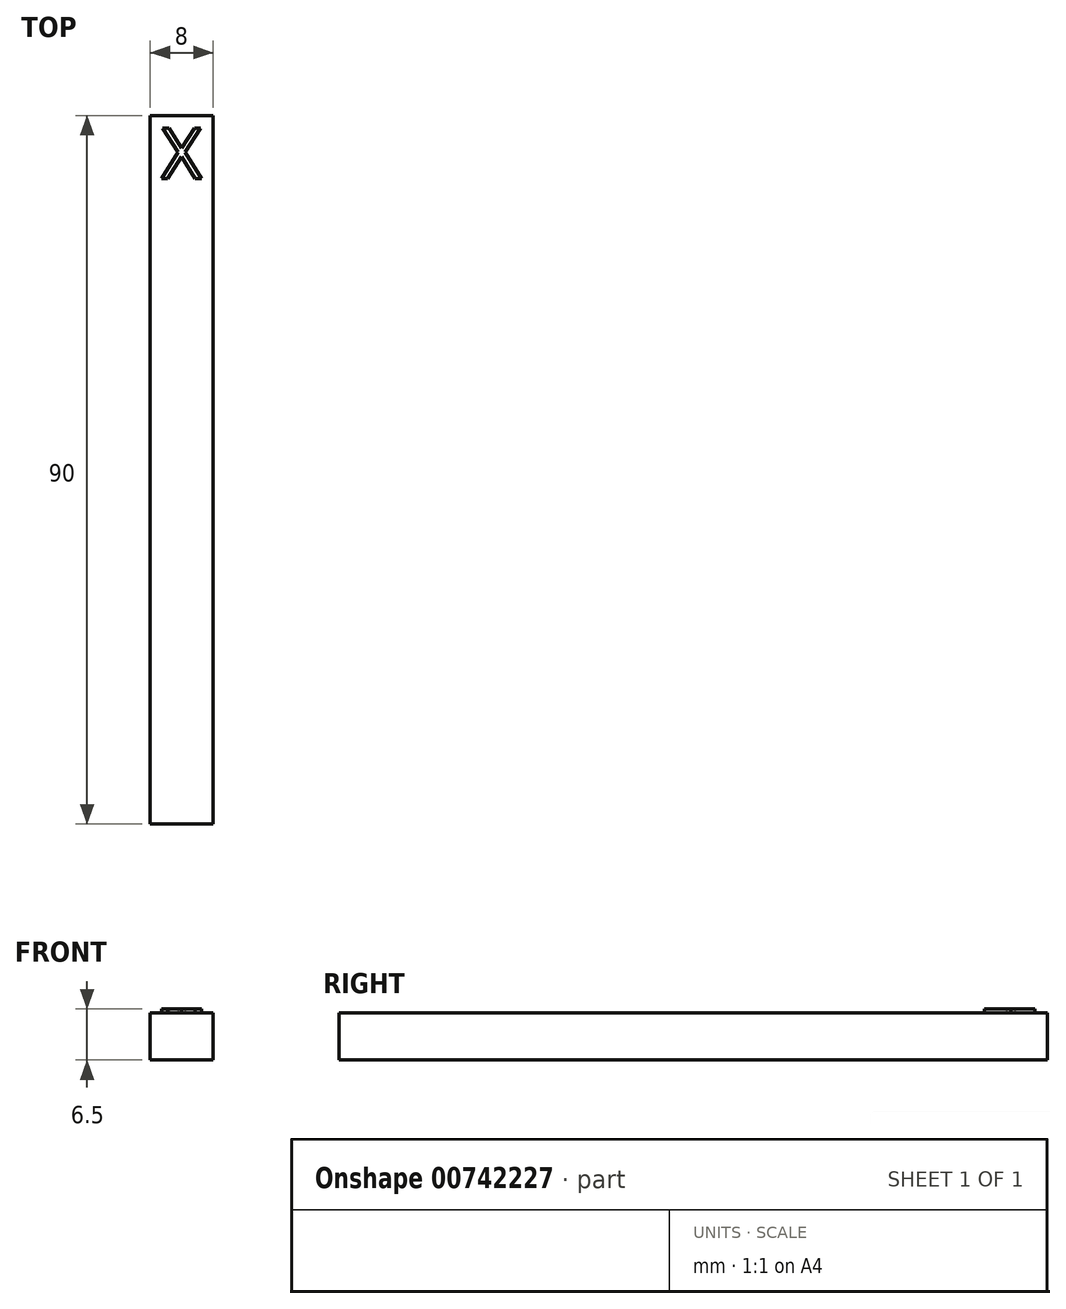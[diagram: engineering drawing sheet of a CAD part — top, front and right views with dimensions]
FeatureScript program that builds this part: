
annotation { "Feature Type Name" : "Feature", "Feature Type Description" : "" }
export const myFeature = defineFeature(function(context is Context, id is Id, definition is map)
    precondition{}
    {
        {
            var Q0;
            Q0=qCreatedBy(makeId("Front.planeOp"),FACE);
            var sketch = newSketch(context, id + "F0", { "sketchPlane" : qUnion([Q0])});
            skLineSegment(sketch, "E0.bottom", {"start": v(4, 3) * mm, "end": v(-4, 3) * mm});
            skLineSegment(sketch, "E0.top", {"start": v(4, -3) * mm, "end": v(-4, -3) * mm});
            skLineSegment(sketch, "E0.left", {"start": v(4, 3) * mm, "end": v(4, -3) * mm});
            skLineSegment(sketch, "E0.right", {"start": v(-4, 3) * mm, "end": v(-4, -3) * mm});
            skPoint(sketch, "E0.middle", {"position": v(0, 0) * mm});
            skSolve(sketch);
        }
        {
            var Q0;
            Q0 = qSketchRegion(id + "F0", true);
            extrude(context, id + "F1", {"entities" : qUnion([Q0]), "depth" : 90 * mm, "offsetDistance" : 25 * mm});
        }
        {
            var Q0;
            Q0=makeQuery(id+"F1.opExtrude","SWEPT_FACE",FACE,{"disambiguationData":[OSD([sQuery(id+"F0.wireOp",EDGE,"E0.bottom")])]});
            var sketch = newSketch(context, id + "F2", { "sketchPlane" : qUnion([Q0])});
            skText(sketch, "E1", { "text": "X", "fontName": "OpenSans-Regular.ttf"});
            const initialGuessF2  = {"E1": [-0.00261, -0.00804, 1, 0, 0.0065]};
            skSetInitialGuess(sketch, initialGuessF2);
            skSolve(sketch);
        }
        {
            var Q0;
            Q0 = qSketchRegion(id + "F2", true);
            extrude(context, id + "F3", {"entities" : qUnion([Q0]), "operationType" : NewBodyOperationType.ADD, "depth" : .5 * mm, "offsetDistance" : 25 * mm});
        }
    });
